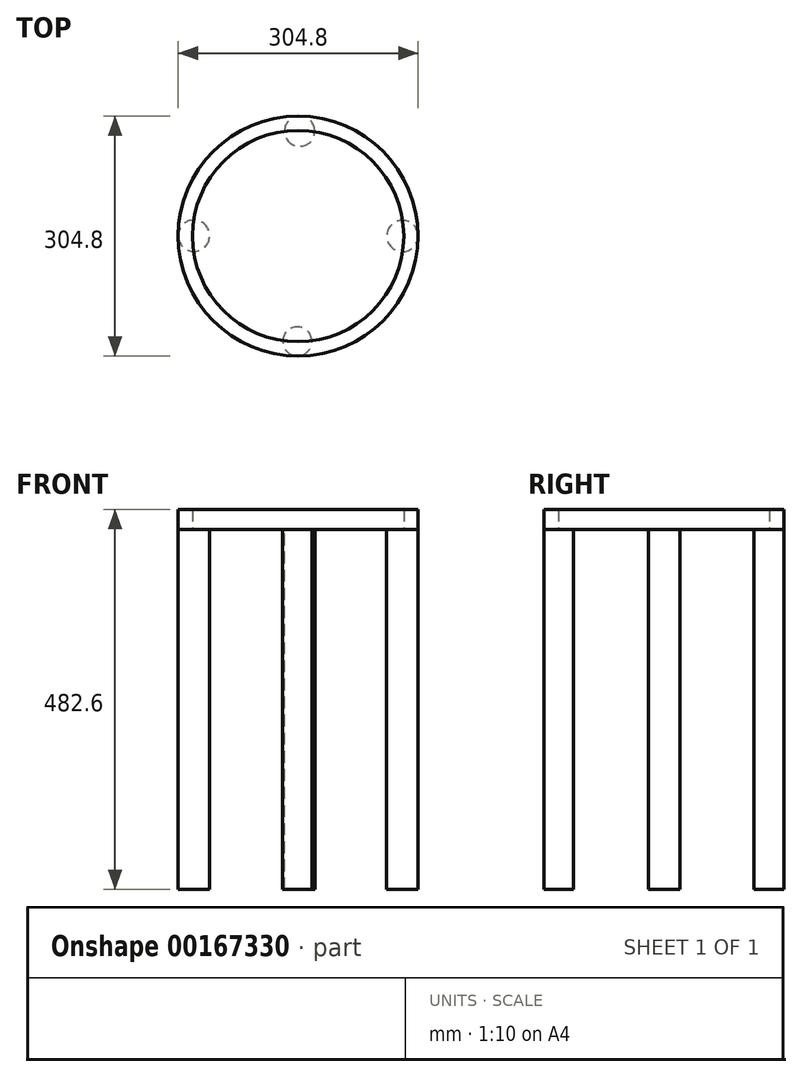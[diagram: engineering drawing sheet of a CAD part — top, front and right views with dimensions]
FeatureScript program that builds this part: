
annotation { "Feature Type Name" : "Feature", "Feature Type Description" : "" }
export const myFeature = defineFeature(function(context is Context, id is Id, definition is map)
    precondition{}
    {
        {
            var Q0;
            Q0=qCreatedBy(makeId("Top.planeOp"),FACE);
            var sketch = newSketch(context, id + "F0", { "sketchPlane" : qUnion([Q0])});
            skCircle(sketch, "E0", {"center": v(0, 0) * mm, "radius": 152.4 * mm});
            skLineSegment(sketch, "E1", {"start": v(-152.4, 0) * mm, "end": v(152.4, 0) * mm});
            skSolve(sketch);
        }
        {
            var Q0;
            Q0 = qSketchRegion(id + "F0", true);
            extrude(context, id + "F1", {"entities" : qUnion([Q0]), "depth" : 25.4 * mm});
        }
        {
            var Q0;
            Q0=makeQuery(id+"F1.opExtrude","CAP_FACE",FACE,{"disambiguationData":[OSD([sQuery(id+"F0.wireOp",EDGE,"E0")])],"isStart":true});
            var sketch = newSketch(context, id + "F2", { "sketchPlane" : qUnion([Q0])});
            skCircle(sketch, "E2", {"center": v(1.92, -133.14) * mm, "radius": 19.25 * mm});
            skLineSegment(sketch, "E3", {"start": v(-17.33, -132.84) * mm, "end": v(21.17, -133.14) * mm});
            skCircle(sketch, "E4", {"center": v(-1.03, 133.87) * mm, "radius": 18.52 * mm});
            skLineSegment(sketch, "E5", {"start": v(-19.55, 134.16) * mm, "end": v(17.5, 133.87) * mm});
            skCircle(sketch, "E6", {"center": v(132.46, -0.1) * mm, "radius": 19.94 * mm});
            skLineSegment(sketch, "E7", {"start": v(112.52, -0.1) * mm, "end": v(152.4, -0.1) * mm});
            skCircle(sketch, "E8", {"center": v(-132.46, -0.42) * mm, "radius": 19.94 * mm});
            skLineSegment(sketch, "E9", {"start": v(-112.52, -0.42) * mm, "end": v(-112.52, -0.42) * mm});
            skLineSegment(sketch, "E10", {"start": v(-112.52, -0.42) * mm, "end": v(-152.4, -0.42) * mm});
            skSolve(sketch);
        }
        {
            var Q0;
            Q0 = qSketchRegion(id + "F2", true);
            extrude(context, id + "F3", {"entities" : qUnion([Q0]), "depth" : 457.2 * mm});
        }
        {
            var Q0;
            Q0=makeQuery(id+"F1.opExtrude","CAP_FACE",FACE,{"disambiguationData":[OSD([sQuery(id+"F0.wireOp",EDGE,"E0")])],"isStart":true});
            var sketch = newSketch(context, id + "F4", { "sketchPlane" : qUnion([Q0])});
            skCircle(sketch, "E11", {"center": v(0, 0) * mm, "radius": 134.19 * mm});
            skSolve(sketch);
        }
        {
            var Q0;
            Q0 = qSketchRegion(id + "F4", true);
            extrude(context, id + "F5", {"entities" : qUnion([Q0]), "oppositeDirection" : true, "depth" : 25.4 * mm});
        }
    });
